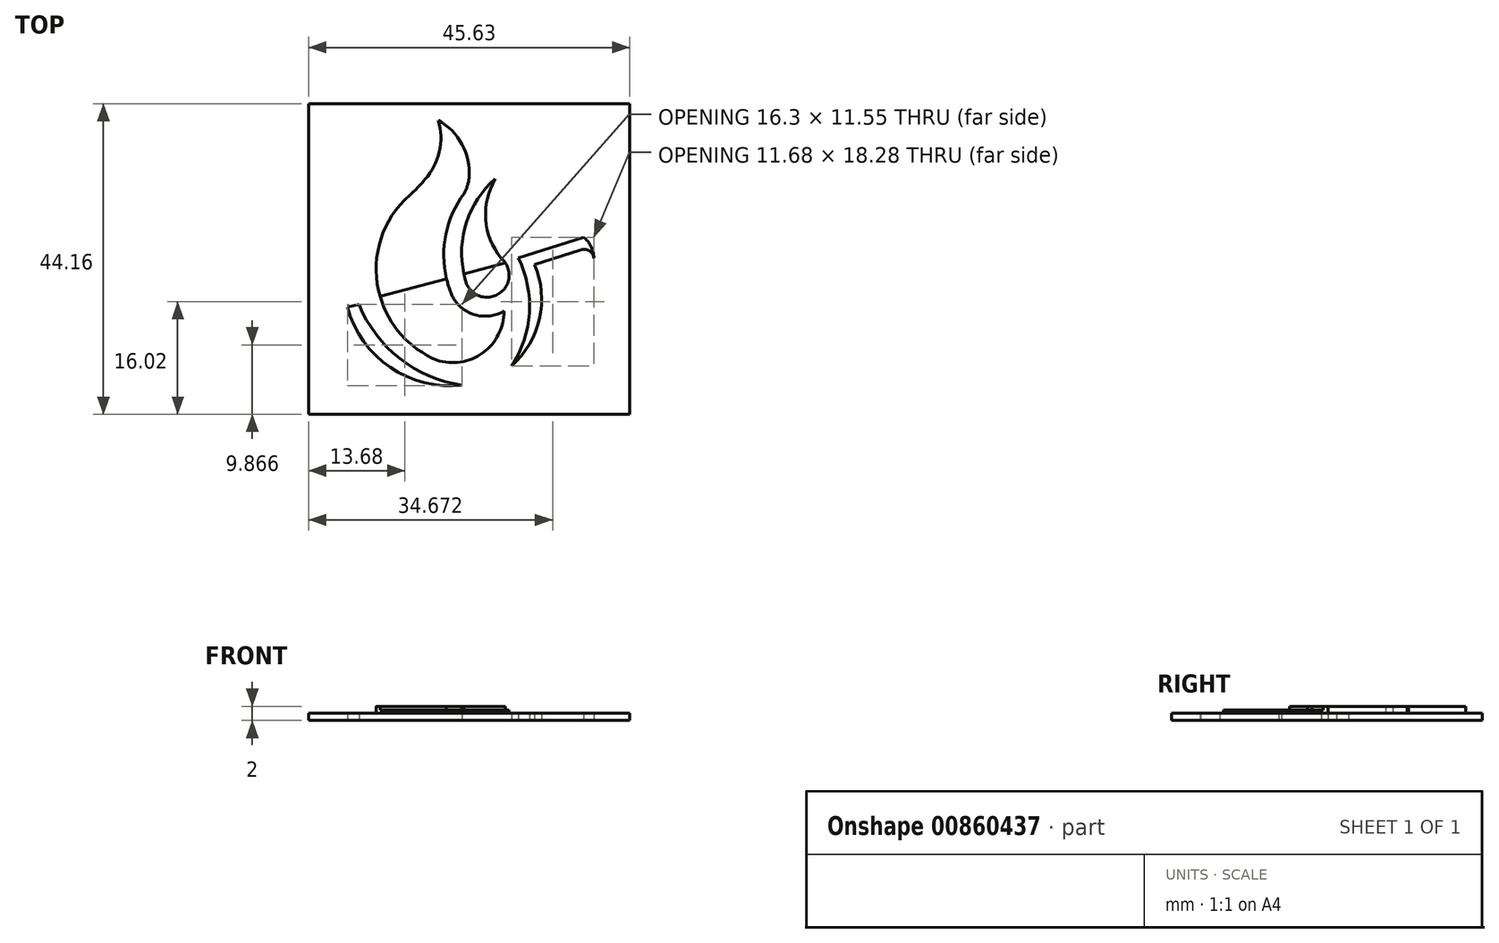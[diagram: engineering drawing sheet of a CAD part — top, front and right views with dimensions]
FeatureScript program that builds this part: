
annotation { "Feature Type Name" : "Feature", "Feature Type Description" : "" }
export const myFeature = defineFeature(function(context is Context, id is Id, definition is map)
    precondition{}
    {
        {
            var Q0;
            Q0=qCreatedBy(makeId("Top.planeOp"),FACE);
            var sketch = newSketch(context, id + "F0", { "sketchPlane" : qUnion([Q0])});
            skPoint(sketch, "E0.orphan", {"position": v(0, 9.7) * mm});
            skPoint(sketch, "E1.center.orphan", {"position": v(3.37, 0) * mm});
            skArc(sketch, "E2", {"start": v(0.36, -1.86) * mm, "mid": v(5, -4.3) * mm, "end": v(5.51, 0.92) * mm});
            skArc(sketch, "E3", {"start": v(4.7, 12.16) * mm, "mid": v(0.54, 5.76) * mm, "end": v(0.36, -1.86) * mm});
            skArc(sketch, "E4", {"start": v(4.7, 12.16) * mm, "mid": v(3.33, 6.4) * mm, "end": v(5.51, 0.92) * mm});
            skArc(sketch, "E5", {"start": v(-4.25, 7) * mm, "mid": v(-4.3, 6.96) * mm, "end": v(-4.36, 6.92) * mm});
            skPoint(sketch, "E6.orphan", {"position": v(-16.38, -13.79) * mm});
            skPoint(sketch, "E7.orphan", {"position": v(15.62, -13.8) * mm});
            skPoint(sketch, "E8.orphan", {"position": v(0, -12.9) * mm});
            skPoint(sketch, "E9.orphan", {"position": v(-16.38, 0) * mm});
            skPoint(sketch, "E10.orphan", {"position": v(15.62, 0) * mm});
            skPoint(sketch, "E11.orphan", {"position": v(-8.38, -3.29) * mm});
            skPoint(sketch, "E12.orphan", {"position": v(-8.53, -3.29) * mm});
            skLineSegment(sketch, "E13.bottom", {"start": v(-21.83, 22.86) * mm, "end": v(23.8, 22.86) * mm});
            skLineSegment(sketch, "E13.top", {"start": v(-21.83, -21.3) * mm, "end": v(23.8, -21.3) * mm});
            skLineSegment(sketch, "E13.left", {"start": v(-21.83, 22.86) * mm, "end": v(-21.83, -21.3) * mm});
            skLineSegment(sketch, "E13.right", {"start": v(23.8, 22.86) * mm, "end": v(23.8, -21.3) * mm});
            skArc(sketch, "E14", {"start": v(-5.31, 12.08) * mm, "mid": v(-3.24, 16.03) * mm, "end": v(-3.39, 20.48) * mm});
            skArc(sketch, "E15", {"start": v(-8.24, 9.14) * mm, "mid": v(-6.71, 10.55) * mm, "end": v(-5.31, 12.08) * mm});
            skArc(sketch, "E16", {"start": v(-8.24, 9.14) * mm, "mid": v(-11.94, -3.45) * mm, "end": v(-3.6, -13.59) * mm});
            skArc(sketch, "E17", {"start": v(0.98, 12.39) * mm, "mid": v(-0.01, 17.08) * mm, "end": v(-3.39, 20.48) * mm});
            skArc(sketch, "E18", {"start": v(0.26, 10.1) * mm, "mid": v(-2.54, 2.83) * mm, "end": v(-1.25, -4.85) * mm});
            skArc(sketch, "E19", {"start": v(-1.25, -4.85) * mm, "mid": v(1.99, -7.2) * mm, "end": v(5.95, -6.65) * mm});
            skArc(sketch, "E20", {"start": v(-3.6, -13.59) * mm, "mid": v(2.93, -12.55) * mm, "end": v(5.95, -6.65) * mm});
            skArc(sketch, "E21", {"start": v(0, 9.7) * mm, "mid": v(0.67, 10.98) * mm, "end": v(0.98, 12.39) * mm});
            skLineSegment(sketch, "E22", {"start": v(-11.66, -4.56) * mm, "end": v(-2.22, -2.02) * mm});
            skLineSegment(sketch, "E23.trimOffspring", {"start": v(0.24, -1.36) * mm, "end": v(6.14, 0.22) * mm});
            skLineSegment(sketch, "E24", {"start": v(-16.3, -6.06) * mm, "end": v(-14.66, -5.66) * mm});
            skArc(sketch, "E25", {"start": v(-14.66, -5.66) * mm, "mid": v(-8.87, -13.37) * mm, "end": v(0, -17.14) * mm});
            skLineSegment(sketch, "E26", {"start": v(7.98, 0.92) * mm, "end": v(17.25, 3.86) * mm});
            skArc(sketch, "E27", {"start": v(18.68, 0.91) * mm, "mid": v(18.3, 2.55) * mm, "end": v(17.25, 3.86) * mm});
            skArc(sketch, "E28", {"start": v(7, -14.42) * mm, "mid": v(9.53, -6.88) * mm, "end": v(7.98, 0.92) * mm});
            skLineSegment(sketch, "E29", {"start": v(10.27, 0) * mm, "end": v(16.87, 2.1) * mm});
            skArc(sketch, "E30", {"start": v(18.68, 0.91) * mm, "mid": v(18.06, 1.93) * mm, "end": v(16.87, 2.1) * mm});
            skArc(sketch, "E31", {"start": v(-16.3, -6.06) * mm, "mid": v(-10.2, -14.62) * mm, "end": v(0, -17.14) * mm});
            skArc(sketch, "E32", {"start": v(7, -14.42) * mm, "mid": v(10.97, -7.74) * mm, "end": v(10.27, 0) * mm});
            skSolve(sketch);
        }
        {
            var Q0;
            Q0=makeQuery(id+"F0.imprint","IMPRINT",FACE,{"disambiguationData":[TD([[makeQuery(id+"F0.imprint","IMPRINT",EDGE,{"derivedFrom":sQuery(id+"F0.wireOp",EDGE,"E13.bottom")}),-1.0]])]});
            var Q1;
            Q1=makeQuery(id+"F0.imprint","IMPRINT",FACE,{"disambiguationData":[TD([[makeQuery(id+"F0.imprint","IMPRINT",EDGE,{"derivedFrom":sQuery(id+"F0.wireOp",EDGE,"E24")}),-1.0]])]});
            var Q2;
            {var subQ7=sQuery(id+"F0.wireOp",EDGE,"E14");Q2=makeQuery(id+"F0.imprint","IMPRINT",FACE,{"disambiguationData":[TD([[makeQuery(id+"F0.imprint","IMPRINT",EDGE,{"derivedFrom":subQ7}),-1.0]])]});}
            var Q3;
            {var subQ1=sQuery(id+"F0.wireOp",EDGE,"E19");Q3=makeQuery(id+"F0.imprint","IMPRINT",FACE,{"disambiguationData":[TD([[makeQuery(id+"F0.imprint","IMPRINT",EDGE,{"derivedFrom":subQ1}),-1.0]])]});}
            var Q4;
            {var subQ3=sQuery(id+"F0.wireOp",EDGE,"E23.trimOffspring");Q4=makeQuery(id+"F0.imprint","IMPRINT",FACE,{"disambiguationData":[TD([[makeQuery(id+"F0.imprint","IMPRINT",EDGE,{"derivedFrom":subQ3}),-1.0]])]});}
            var Q5;
            {var subQ3=sQuery(id+"F0.wireOp",EDGE,"E23.trimOffspring");Q5=makeQuery(id+"F0.imprint","IMPRINT",FACE,{"disambiguationData":[TD([[makeQuery(id+"F0.imprint","IMPRINT",EDGE,{"derivedFrom":subQ3}),1.0]])]});}
            var Q6;
            Q6=makeQuery(id+"F0.imprint","IMPRINT",FACE,{"disambiguationData":[TD([[makeQuery(id+"F0.imprint","IMPRINT",EDGE,{"derivedFrom":sQuery(id+"F0.wireOp",EDGE,"E26")}),-1.0]])]});
            extrude(context, id + "F1", {"entities" : qUnion([Q0, Q1, Q2, Q3, Q4, Q5, Q6]), "depth" : 1 * mm, "offsetDistance" : 25 * mm});
        }
        {
            var Q0;
            Q0=makeQuery(id+"F0.imprint","IMPRINT",FACE,{"disambiguationData":[TD([[makeQuery(id+"F0.imprint","IMPRINT",EDGE,{"derivedFrom":sQuery(id+"F0.wireOp",EDGE,"E14")}),-1.0]])]});
            var Q1;
            {var subQ0=sQuery(id+"F0.wireOp",EDGE,"E4");Q1=makeQuery(id+"F0.imprint","IMPRINT",FACE,{"disambiguationData":[TD([[makeQuery(id+"F0.imprint","IMPRINT",EDGE,{"derivedFrom":subQ0}),-1.0]])]});}
            extrude(context, id + "F2", {"entities" : qUnion([Q0, Q1]), "operationType" : NewBodyOperationType.ADD, "depth" : 2 * mm, "offsetDistance" : 25 * mm});
        }
        {
            var Q0;
            {var subQ0=sQuery(id+"F0.wireOp",EDGE,"E19");Q0=makeQuery(id+"F0.imprint","IMPRINT",FACE,{"disambiguationData":[TD([[makeQuery(id+"F0.imprint","IMPRINT",EDGE,{"derivedFrom":subQ0}),-1.0]])]});}
            var Q1;
            {var subQ3=sQuery(id+"F0.wireOp",EDGE,"E23.trimOffspring");Q1=makeQuery(id+"F0.imprint","IMPRINT",FACE,{"disambiguationData":[TD([[makeQuery(id+"F0.imprint","IMPRINT",EDGE,{"derivedFrom":subQ3}),-1.0]])]});}
            extrude(context, id + "F3", {"entities" : qUnion([Q0, Q1]), "operationType" : NewBodyOperationType.ADD, "depth" : 1.5 * mm, "offsetDistance" : 25 * mm});
        }
        {
            var Q0;
            Q0=makeQuery(id+"F0.imprint","IMPRINT",FACE,{"disambiguationData":[TD([[makeQuery(id+"F0.imprint","IMPRINT",EDGE,{"derivedFrom":sQuery(id+"F0.wireOp",EDGE,"E24")}),-1.0]])]});
            var Q1;
            Q1=makeQuery(id+"F0.imprint","IMPRINT",FACE,{"disambiguationData":[TD([[makeQuery(id+"F0.imprint","IMPRINT",EDGE,{"derivedFrom":sQuery(id+"F0.wireOp",EDGE,"E26")}),-1.0]])]});
            extrude(context, id + "F4", {"entities" : qUnion([Q0, Q1]), "operationType" : NewBodyOperationType.REMOVE, "depth" : 1 * mm, "offsetDistance" : 25 * mm});
        }
    });
